# Revit family: SpecEquip_TMV_Zip_Horne TMV box with bypass pipes both ends
name_source: partatom
category: Specialty Equipment
revit_build: Autodesk Revit 2016 (Build: 20150220_1215(x64)
units: mm (PartAtom-declared; Revit-internal decimal feet)

## family parameters
Always vertical = Yes
Cut with Voids When Loaded = Yes
OmniClass Number = 23.65.55.14.24
OmniClass Title = Mixing Valves for Liquid Services
Part Type = Normal
Room Calculation Point = No
Round Connector Dimension = Use Diameter
Shared = No
Work Plane-Based = No

## types (2) — shared parameters
Manufacturer = Zip Australia
Manufacturer_Overall Depth = 74 mm  [stored 0.242782 ft]
Manufacturer_Overall Height = 370 mm  [stored 1.21391 ft]
Manufacturer_Overall Width = 370 mm  [stored 1.21391 ft]
Manufacturer_URL__Product Specific = https://www.zipwater.com
Material_ANZRS = z_ZipTmv_Chrome
ModifiedIssue_ANZRS = 20171020 $
URL = https://www.zipwater.com

## per-type parameters (varying)
| type | Description | Hinged Door | Manufacturer_Spec Code | Model | Removeable Door | Type Comments |
| TMV Hinged Door | Horne TMV Model H1502: Recessed pre-plumbed box configuration with lockable Hinged stainless steel door and cold water bypass - pipes at both ends | Yes | 42155 | Horne TMV  H1502 Brass in box Configuration - Hinged Door | No | Hinged Door |
| TMV Removable Door | Horne TMV Model H1502: Recessed pre-plumbed box configuration with lockable flat stainless steel removable door and cold water bypass - pipes at both ends | No | 42455 | Horne TMV  H1502 Brass in box Configuration - Removable Door | Yes | Removable Door |

note: [stored X ft] marks values corroborated as IEEE doubles in the binary element streams (Revit-internal decimal feet)

## geometry (parser evidence)
native form markers: Sweep x6
no freeform markers — native parametric forms only
